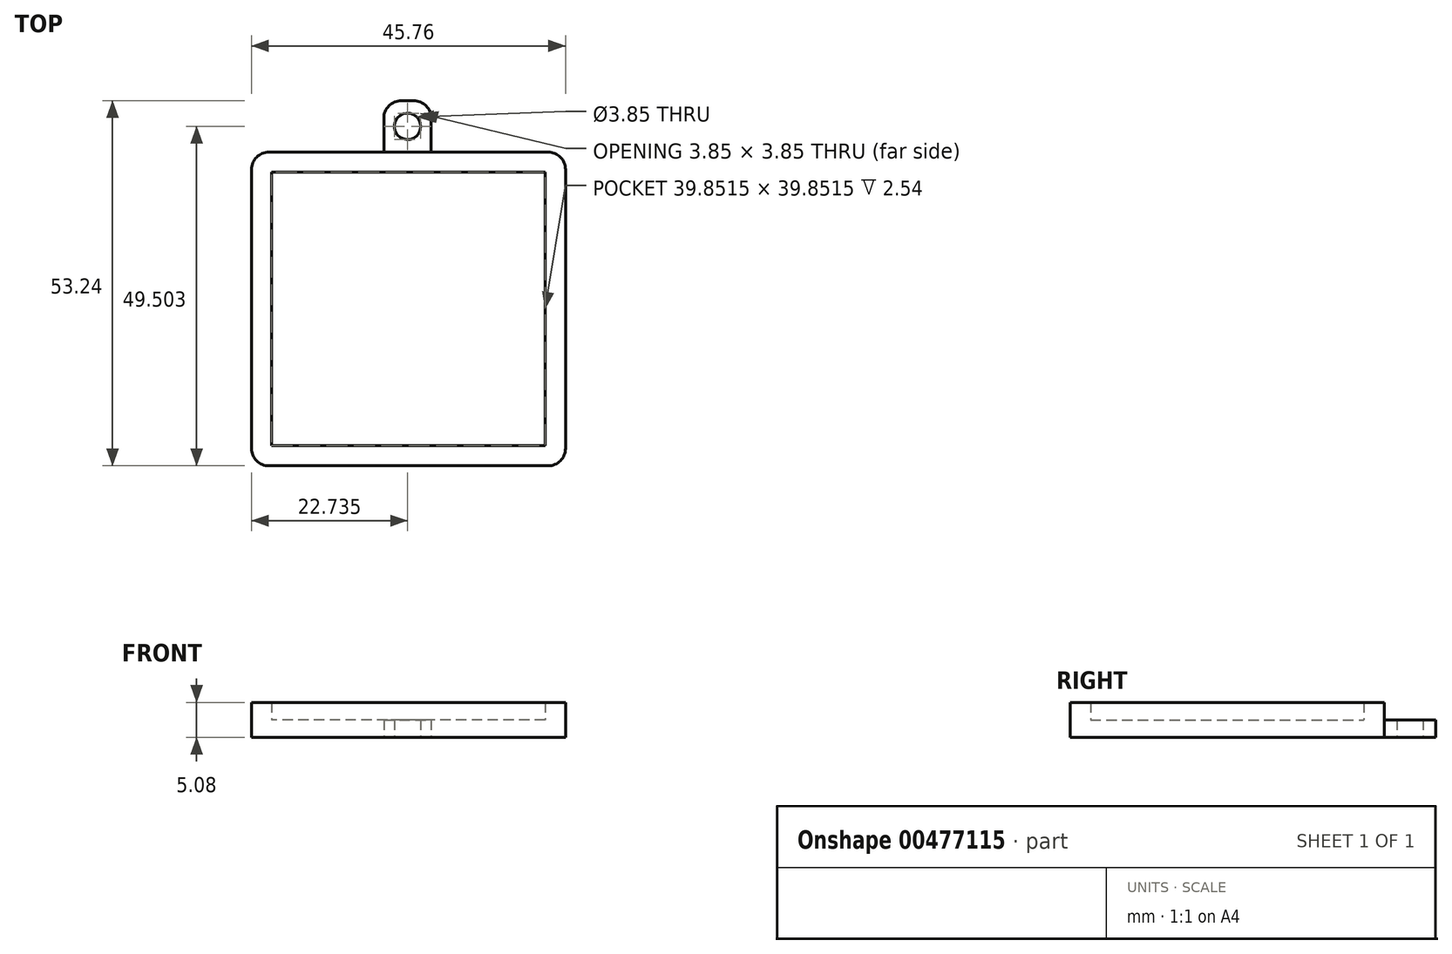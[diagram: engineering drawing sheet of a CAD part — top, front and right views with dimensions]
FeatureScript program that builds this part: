
annotation { "Feature Type Name" : "Feature", "Feature Type Description" : "" }
export const myFeature = defineFeature(function(context is Context, id is Id, definition is map)
    precondition{}
    {
        {
            var Q0;
            Q0=qCreatedBy(makeId("Top.planeOp"),FACE);
            var sketch = newSketch(context, id + "F0", { "sketchPlane" : qUnion([Q0])});
            skLineSegment(sketch, "E0.bottom", {"start": v(0, 0) * mm, "end": v(-45.76, 0) * mm});
            skLineSegment(sketch, "E0.top", {"start": v(0, 45.76) * mm, "end": v(-19.57, 45.76) * mm});
            skLineSegment(sketch, "E0.left", {"start": v(0, 0) * mm, "end": v(0, 45.76) * mm});
            skLineSegment(sketch, "E0.right", {"start": v(-45.76, 0) * mm, "end": v(-45.76, 45.76) * mm});
            skLineSegment(sketch, "E1.right", {"start": v(-19.57, 53.24) * mm, "end": v(-19.57, 45.76) * mm});
            skLineSegment(sketch, "E2.right", {"start": v(-26.48, 53.24) * mm, "end": v(-26.48, 45.76) * mm});
            skLineSegment(sketch, "E3.top", {"start": v(-19.57, 53.24) * mm, "end": v(-26.48, 53.24) * mm});
            skLineSegment(sketch, "E3.left", {"start": v(-19.57, 45.76) * mm, "end": v(-19.57, 53.24) * mm});
            skLineSegment(sketch, "E3.right", {"start": v(-26.48, 45.76) * mm, "end": v(-26.48, 53.24) * mm});
            skPoint(sketch, "E4.start.orphan", {"position": v(-22.88, 22.88) * mm});
            skLineSegment(sketch, "E5.trimOffspring", {"start": v(-26.48, 45.76) * mm, "end": v(-45.76, 45.76) * mm});
            skCircle(sketch, "E6", {"center": v(-23.02, 49.5) * mm, "radius": 1.93 * mm});
            skSolve(sketch);
        }
        {
            var Q0;
            Q0 = qSketchRegion(id + "F0", true);
            extrude(context, id + "F1", {"entities" : qUnion([Q0]), "depth" : 2.54 * mm});
        }
        {
            var Q0;
            Q0=makeQuery(id+"F1.opExtrude","CAP_FACE",FACE,{"disambiguationData":[OSD([sQuery(id+"F0.wireOp",EDGE,"E0.bottom"),sQuery(id+"F0.wireOp",EDGE,"E0.top"),sQuery(id+"F0.wireOp",EDGE,"E0.left"),sQuery(id+"F0.wireOp",EDGE,"E0.right"),sQuery(id+"F0.wireOp",EDGE,"E3.top"),sQuery(id+"F0.wireOp",EDGE,"E3.left"),sQuery(id+"F0.wireOp",EDGE,"E3.right"),sQuery(id+"F0.wireOp",EDGE,"E5.trimOffspring"),sQuery(id+"F0.wireOp",EDGE,"E6")])],"isStart":false});
            var sketch = newSketch(context, id + "F2", { "sketchPlane" : qUnion([Q0])});
            skPoint(sketch, "E7.endSnap0", {"position": v(-22.88, 22.88) * mm});
            skLineSegment(sketch, "E8", {"start": v(-42.8, 42.8) * mm, "end": v(-2.95, 42.8) * mm});
            skLineSegment(sketch, "E9", {"start": v(-2.95, 2.95) * mm, "end": v(-42.8, 2.95) * mm});
            skLineSegment(sketch, "E10", {"start": v(-42.8, 2.95) * mm, "end": v(-42.8, 42.8) * mm});
            skLineSegment(sketch, "E11", {"start": v(-2.95, 2.95) * mm, "end": v(-2.95, 42.8) * mm});
            skPoint(sketch, "E12.orphan", {"position": v(-2.95, -9.11) * mm});
            skPoint(sketch, "E13.orphan", {"position": v(-42.8, -9.11) * mm});
            skPoint(sketch, "E14.trimOffspring.end.orphan", {"position": v(0, 45.76) * mm});
            skPoint(sketch, "E15.start.orphan", {"position": v(-45.76, 0) * mm});
            skLineSegment(sketch, "E16.bottom", {"start": v(-45.76, 0) * mm, "end": v(0, 0) * mm});
            skLineSegment(sketch, "E16.top", {"start": v(-45.76, 45.76) * mm, "end": v(0, 45.76) * mm});
            skLineSegment(sketch, "E16.left", {"start": v(-45.76, 0) * mm, "end": v(-45.76, 45.76) * mm});
            skLineSegment(sketch, "E16.right", {"start": v(0, 0) * mm, "end": v(0, 45.76) * mm});
            skPoint(sketch, "E17.orphan", {"position": v(-22.88, 59.3) * mm});
            skSolve(sketch);
        }
        {
            var Q0;
            Q0 = qSketchRegion(id + "F2", true);
            extrude(context, id + "F3", {"entities" : qUnion([Q0]), "operationType" : NewBodyOperationType.ADD, "depth" : 2.54 * mm});
        }
        {
            var Q0;
            {var subQ0=sQuery(id+"F0.wireOp",EDGE,"E3.left");var subQ1=sQuery(id+"F0.wireOp",EDGE,"E3.top");var subQ2=sQuery(id+"F0.wireOp",EDGE,"E3.right");var subQ3=sQuery(id+"F0.wireOp",EDGE,"E0.top");var subQ4=sQuery(id+"F0.wireOp",EDGE,"E5.trimOffspring");var subQ5=sQuery(id+"F0.wireOp",EDGE,"E6");Q0=makeQuery(id+"F3.boolean.opBoolean","SPLIT",FACE,{"disambiguationData":[TD([makeQuery(id+"F1.opExtrude","SWEPT_FACE",FACE,{"disambiguationData":[OSD([subQ3])]})])],"derivedFrom":makeQuery(id+"F1.opExtrude","CAP_FACE",FACE,{"disambiguationData":[OSD([sQuery(id+"F0.wireOp",EDGE,"E0.bottom"),subQ3,sQuery(id+"F0.wireOp",EDGE,"E0.left"),sQuery(id+"F0.wireOp",EDGE,"E0.right"),subQ1,subQ0,subQ2,subQ4,subQ5])],"isStart":false})});}
            var sketch = newSketch(context, id + "F4", { "sketchPlane" : qUnion([Q0])});
            skLineSegment(sketch, "E18", {"start": v(-26.48, 45.76) * mm, "end": v(-19.57, 53.24) * mm});
            skLineSegment(sketch, "E19", {"start": v(-19.57, 45.76) * mm, "end": v(-26.48, 53.24) * mm});
            skLineSegment(sketch, "E20", {"start": v(-26.48, 53.24) * mm, "end": v(-21.72, 48.09) * mm});
            skPoint(sketch, "E21", {"position": v(-23.02, 49.5) * mm});
            skSolve(sketch);
        }
        {
            var Q0;
            Q0=sQuery(id+"F4.wireOp",VERTEX,"E21");
            var Q1;
            Q1=makeQuery(id+"F1.opExtrude","SWEPT_BODY",BODY,{"disambiguationData":[OSD([sQuery(id+"F0.wireOp",EDGE,"E0.bottom"),sQuery(id+"F0.wireOp",EDGE,"E0.top"),sQuery(id+"F0.wireOp",EDGE,"E0.left"),sQuery(id+"F0.wireOp",EDGE,"E0.right"),sQuery(id+"F0.wireOp",EDGE,"E3.top"),sQuery(id+"F0.wireOp",EDGE,"E3.left"),sQuery(id+"F0.wireOp",EDGE,"E3.right"),sQuery(id+"F0.wireOp",EDGE,"E5.trimOffspring"),sQuery(id+"F0.wireOp",EDGE,"E6")])]});
            hole(context, id + "F5", {"style" : HoleStyle.SIMPLE, "endStyle" : HoleEndStyle.BLIND, "holeDiameter" : 3.86 * mm, "holeDepth" : 12.7 * mm, "isTappedThrough" : true, "tappedDepth" : 12.7 * mm, "tapClearance" : 3, "locations" : qUnion([Q0]), "scope" : qUnion([Q1])});
        }
        {
            var Q0;
            Q0=makeQuery(id+"F1.opExtrude","SWEPT_EDGE",EDGE,{"disambiguationData":[OSD([sQuery(id+"F0.wireOp",EDGE,"E3.top"),sQuery(id+"F0.wireOp",EDGE,"E3.left")])]});
            var Q1;
            Q1=makeQuery(id+"F1.opExtrude","SWEPT_EDGE",EDGE,{"disambiguationData":[OSD([sQuery(id+"F0.wireOp",EDGE,"E3.top"),sQuery(id+"F0.wireOp",EDGE,"E3.right")])]});
            var Q2;
            Q2=makeQuery(id+"F3.boolean.opBoolean","MERGE",EDGE,{"derivedFrom":[makeQuery(id+"F1.opExtrude","SWEPT_EDGE",EDGE,{"disambiguationData":[OSD([sQuery(id+"F0.wireOp",EDGE,"E0.top"),sQuery(id+"F0.wireOp",EDGE,"E0.left")])]}),makeQuery(id+"F3.opExtrude","SWEPT_EDGE",EDGE,{"disambiguationData":[OSD([sQuery(id+"F2.wireOp",EDGE,"E16.top"),sQuery(id+"F2.wireOp",EDGE,"E16.right")])]})]});
            var Q3;
            Q3=makeQuery(id+"F3.boolean.opBoolean","MERGE",EDGE,{"derivedFrom":[makeQuery(id+"F1.opExtrude","SWEPT_EDGE",EDGE,{"disambiguationData":[OSD([sQuery(id+"F0.wireOp",EDGE,"E0.bottom"),sQuery(id+"F0.wireOp",EDGE,"E0.left")])]}),makeQuery(id+"F3.opExtrude","SWEPT_EDGE",EDGE,{"disambiguationData":[OSD([sQuery(id+"F2.wireOp",EDGE,"E16.bottom"),sQuery(id+"F2.wireOp",EDGE,"E16.right")])]})]});
            var Q4;
            Q4=makeQuery(id+"F3.boolean.opBoolean","MERGE",EDGE,{"derivedFrom":[makeQuery(id+"F1.opExtrude","SWEPT_EDGE",EDGE,{"disambiguationData":[OSD([sQuery(id+"F0.wireOp",EDGE,"E0.bottom"),sQuery(id+"F0.wireOp",EDGE,"E0.right")])]}),makeQuery(id+"F3.opExtrude","SWEPT_EDGE",EDGE,{"disambiguationData":[OSD([sQuery(id+"F2.wireOp",EDGE,"E16.bottom"),sQuery(id+"F2.wireOp",EDGE,"E16.left")])]})]});
            var Q5;
            Q5=makeQuery(id+"F3.boolean.opBoolean","MERGE",EDGE,{"derivedFrom":[makeQuery(id+"F1.opExtrude","SWEPT_EDGE",EDGE,{"disambiguationData":[OSD([sQuery(id+"F0.wireOp",EDGE,"E0.right"),sQuery(id+"F0.wireOp",EDGE,"E5.trimOffspring")])]}),makeQuery(id+"F3.opExtrude","SWEPT_EDGE",EDGE,{"disambiguationData":[OSD([sQuery(id+"F2.wireOp",EDGE,"E16.top"),sQuery(id+"F2.wireOp",EDGE,"E16.left")])]})]});
            fillet(context, id + "F6", {"entities" : qUnion([Q0, Q1, Q2, Q3, Q4, Q5]), "radius" : 2.54 * mm, "tangentPropagation" : true, "allowEdgeOverflow" : false});
        }
    });
